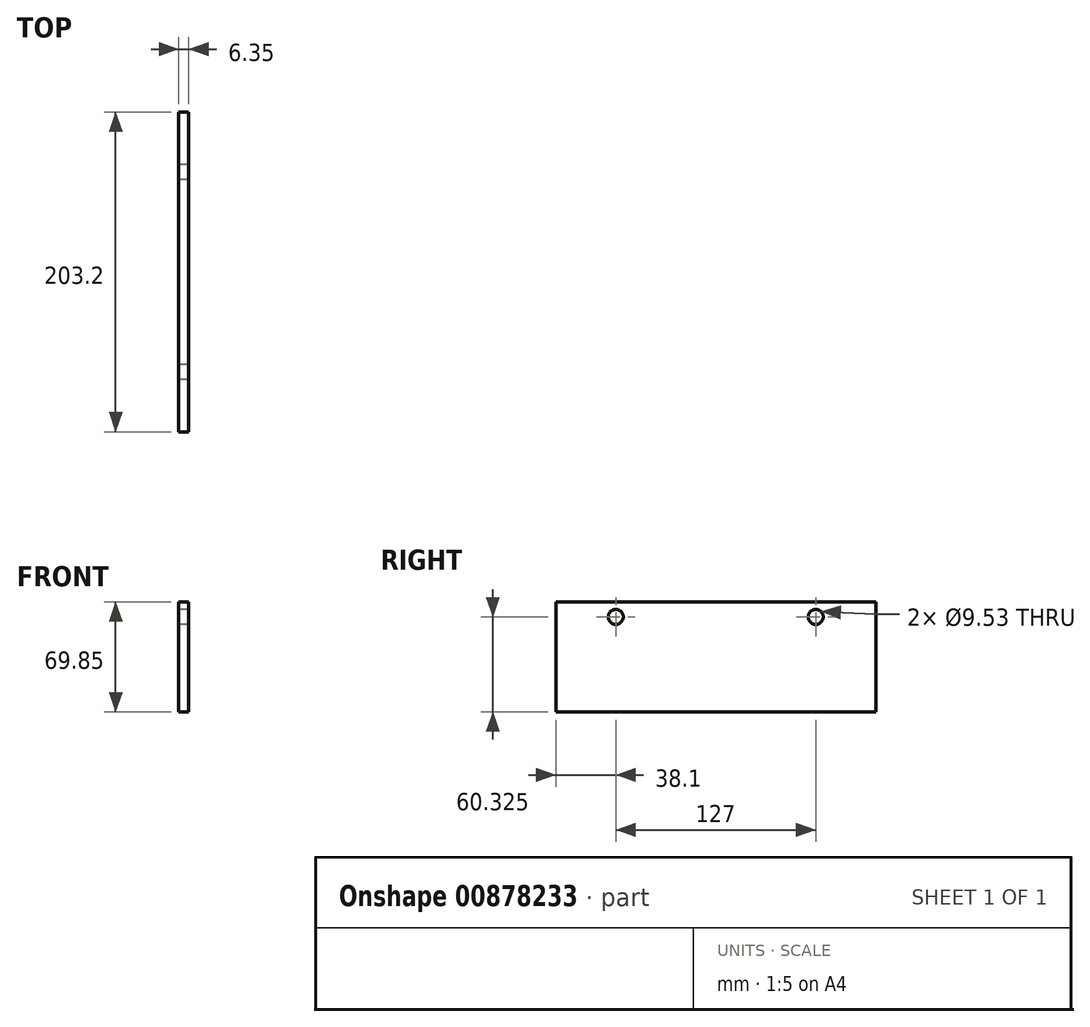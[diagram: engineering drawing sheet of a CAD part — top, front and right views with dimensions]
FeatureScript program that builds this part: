
annotation { "Feature Type Name" : "Feature", "Feature Type Description" : "" }
export const myFeature = defineFeature(function(context is Context, id is Id, definition is map)
    precondition{}
    {
        {
            var Q0;
            Q0=qCreatedBy(makeId("Right.planeOp"),FACE);
            var sketch = newSketch(context, id + "F0", { "sketchPlane" : qUnion([Q0])});
            skLineSegment(sketch, "E0.bottom", {"start": v(0, 0) * mm, "end": v(203.2, 0) * mm});
            skLineSegment(sketch, "E0.top", {"start": v(0, 69.85) * mm, "end": v(203.2, 69.85) * mm});
            skLineSegment(sketch, "E0.left", {"start": v(0, 0) * mm, "end": v(0, 69.85) * mm});
            skLineSegment(sketch, "E0.right", {"start": v(203.2, 0) * mm, "end": v(203.2, 69.85) * mm});
            skCircle(sketch, "E1", {"center": v(38.1, 60.33) * mm, "radius": 4.76 * mm});
            skLineSegment(sketch, "E2", {"start": v(101.6, 69.85) * mm, "end": v(101.6, 0) * mm, "construction": true});
            skCircle(sketch, "E3.MirrorC", {"center": v(165.1, 60.33) * mm, "radius": 4.76 * mm});
            skSolve(sketch);
        }
        {
            var Q0;
            Q0=makeQuery(id+"F0.imprint","IMPRINT",FACE,{"disambiguationData":[TD([[makeQuery(id+"F0.imprint","IMPRINT",EDGE,{"derivedFrom":sQuery(id+"F0.wireOp",EDGE,"E0.bottom")}),1.0]])]});
            extrude(context, id + "F1", {"entities" : qUnion([Q0]), "depth" : 6.35 * mm, "offsetDistance" : 25.4 * mm});
        }
    });
